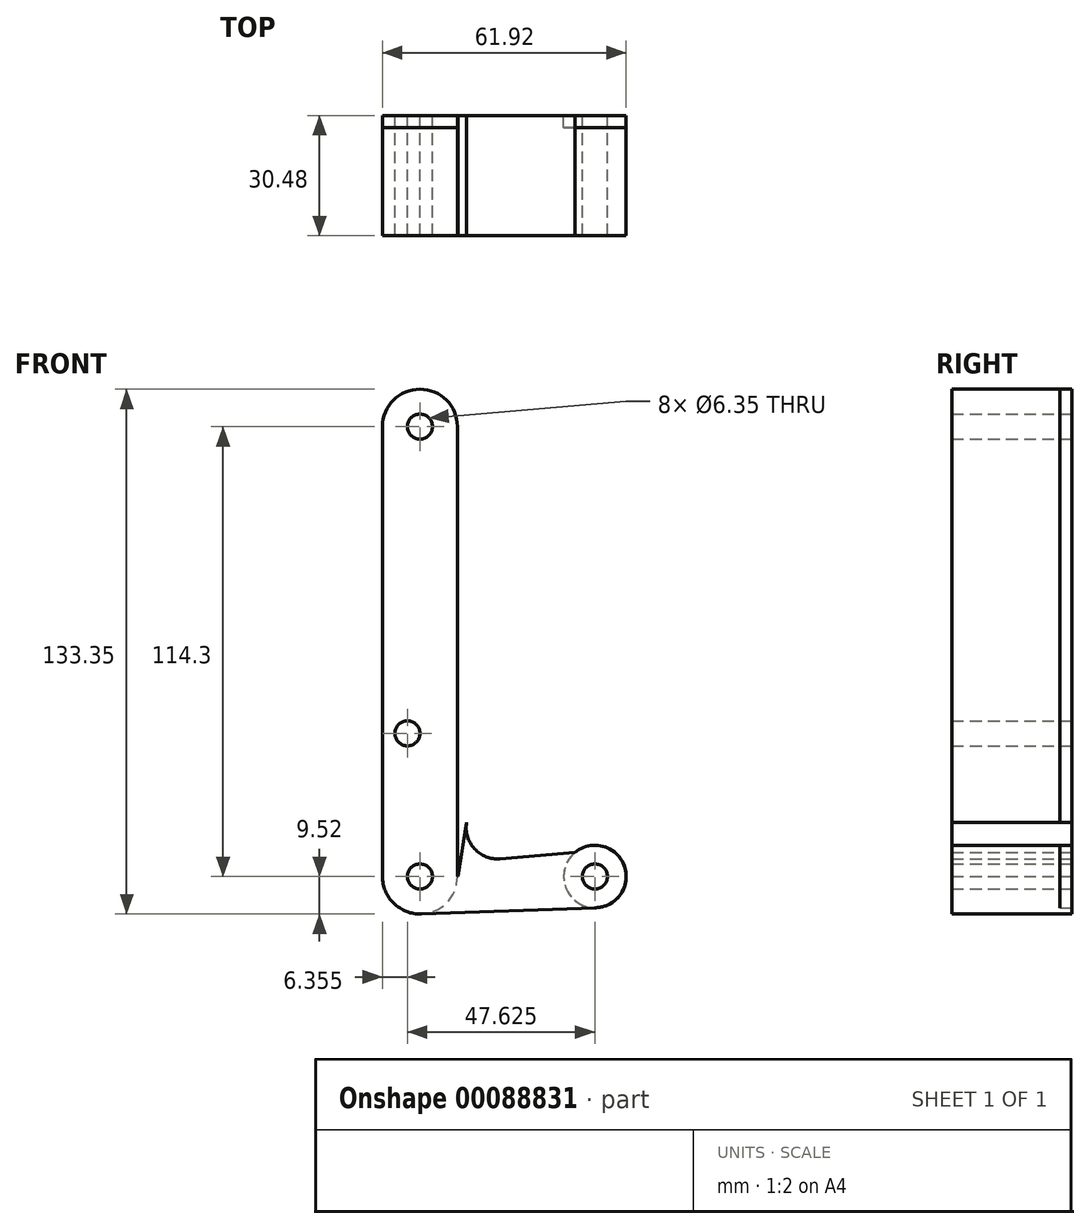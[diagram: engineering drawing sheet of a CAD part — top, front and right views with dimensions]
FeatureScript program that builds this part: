
annotation { "Feature Type Name" : "Feature", "Feature Type Description" : "" }
export const myFeature = defineFeature(function(context is Context, id is Id, definition is map)
    precondition{}
    {
        {
            var Q0;
            Q0=qCreatedBy(makeId("Front.planeOp"),FACE);
            var sketch = newSketch(context, id + "F0", { "sketchPlane" : qUnion([Q0])});
            skCircle(sketch, "E0", {"center": v(0, 114.3) * mm, "radius": 9.53 * mm});
            skCircle(sketch, "E1", {"center": v(0, 0) * mm, "radius": 9.53 * mm});
            skLineSegment(sketch, "E2", {"start": v(0, 114.3) * mm, "end": v(0, 0) * mm, "construction": true});
            skLineSegment(sketch, "E3", {"start": v(0, 0) * mm, "end": v(0, 0) * mm});
            skCircle(sketch, "E4", {"center": v(44.45, 0) * mm, "radius": 7.94 * mm});
            skLineSegment(sketch, "E5", {"start": v(0, 0) * mm, "end": v(44.45, 0) * mm, "construction": true});
            skLineSegment(sketch, "E6", {"start": v(-9.53, 114.3) * mm, "end": v(9.53, 114.3) * mm, "construction": true});
            skLineSegment(sketch, "E7", {"start": v(36.51, 0) * mm, "end": v(52.39, 0) * mm, "construction": true});
            skCircle(sketch, "E8", {"center": v(-3.17, 36.39) * mm, "radius": 3.18 * mm});
            skCircle(sketch, "E9", {"center": v(0, 114.3) * mm, "radius": 3.18 * mm});
            skCircle(sketch, "E10", {"center": v(0, 0) * mm, "radius": 3.18 * mm});
            skCircle(sketch, "E11", {"center": v(44.45, 0) * mm, "radius": 3.18 * mm});
            skLineSegment(sketch, "E12", {"start": v(0, 0) * mm, "end": v(-9.52, 0) * mm, "construction": true});
            skLineSegment(sketch, "E13", {"start": v(44.45, 0) * mm, "end": v(44.45, 7.94) * mm, "construction": true});
            skLineSegment(sketch, "E14", {"start": v(44.45, 0) * mm, "end": v(44.45, -7.94) * mm, "construction": true});
            skLineSegment(sketch, "E15", {"start": v(0, 0) * mm, "end": v(0, -9.52) * mm, "construction": true});
            skLineSegment(sketch, "E16", {"start": v(-9.48, -0.95) * mm, "end": v(-9.48, -0.95) * mm});
            skLineSegment(sketch, "E17", {"start": v(-9.53, 0) * mm, "end": v(-9.53, 114.3) * mm});
            skLineSegment(sketch, "E18", {"start": v(9.52, 114.3) * mm, "end": v(9.53, 0) * mm});
            skLineSegment(sketch, "E19", {"start": v(0.34, -9.52) * mm, "end": v(44.73, -7.93) * mm});
            skLineSegment(sketch, "E20", {"start": v(-29.5, 0) * mm, "end": v(-9.52, 0) * mm, "construction": true});
            skLineSegment(sketch, "E21", {"start": v(-9.53, 0) * mm, "end": v(15.62, 0) * mm});
            skLineSegment(sketch, "E22", {"start": v(11.85, 13.7) * mm, "end": v(9.4, -1.51) * mm});
            skLineSegment(sketch, "E23", {"start": v(20.37, 4.51) * mm, "end": v(39.39, 6.11) * mm});
            skArc(sketch, "E24.filletArc", {"start": v(11.85, 13.7) * mm, "mid": v(13.87, 7.03) * mm, "end": v(20.37, 4.51) * mm});
            skSolve(sketch);
        }
        {
            var Q0;
            {var subQ0=sQuery(id+"F0.wireOp",EDGE,"WO3eCZr5-fNXB-MPyK-c7Pb-Blm2dAQ9tnTr");var subQ1=sQuery(id+"F0.wireOp",EDGE,"E1");var subQ3=makeQuery(id+"F0.imprint","INTERSECT",VERTEX,{"derivedFrom":[subQ1,subQ0]});Q0=makeQuery(id+"F0.imprint","IMPRINT",FACE,{"disambiguationData":[TD([[makeQuery(id+"F0.imprint","IMPRINT",EDGE,{"disambiguationData":[TD([[subQ3,-1.0]])],"derivedFrom":subQ1}),1.0]])]});}
            var Q1;
            {var subQ0=sQuery(id+"F0.wireOp",EDGE,"HDLuu1hv-UhLx-1RbK-1B1E-SFA8OtgyVLiV");var subQ1=sQuery(id+"F0.wireOp",EDGE,"E1");var subQ3=makeQuery(id+"F0.imprint","INTERSECT",VERTEX,{"derivedFrom":[subQ1,subQ0]});Q1=makeQuery(id+"F0.imprint","IMPRINT",FACE,{"disambiguationData":[TD([[makeQuery(id+"F0.imprint","IMPRINT",EDGE,{"disambiguationData":[TD([[subQ3,1.0]])],"derivedFrom":subQ1}),1.0]])]});}
            var Q2;
            Q2=makeQuery(id+"F0.imprint","IMPRINT",FACE,{"disambiguationData":[TD([[makeQuery(id+"F0.imprint","IMPRINT",EDGE,{"derivedFrom":sQuery(id+"F0.wireOp",EDGE,"E9")}),-1.0]])]});
            var Q3;
            Q3=makeQuery(id+"F0.imprint","IMPRINT",FACE,{"disambiguationData":[TD([[makeQuery(id+"F0.imprint","IMPRINT",EDGE,{"derivedFrom":sQuery(id+"F0.wireOp",EDGE,"E10")}),-1.0]])]});
            var Q4;
            Q4=makeQuery(id+"F0.imprint","IMPRINT",FACE,{"disambiguationData":[TD([[makeQuery(id+"F0.imprint","IMPRINT",EDGE,{"derivedFrom":sQuery(id+"F0.wireOp",EDGE,"E11")}),-1.0]])]});
            var Q5;
            {var subQ0=sQuery(id+"F0.wireOp",EDGE,"WrntBw47-ybk8-7ETv-zcuC-ZTsZzzl9P6jG");Q5=makeQuery(id+"F0.imprint","IMPRINT",FACE,{"disambiguationData":[TD([[makeQuery(id+"F0.imprint","IMPRINT",EDGE,{"derivedFrom":subQ0}),-1.0]])]});}
            var Q6;
            Q6=makeQuery(id+"F0.imprint","IMPRINT",FACE,{"disambiguationData":[TD([[makeQuery(id+"F0.imprint","IMPRINT",EDGE,{"derivedFrom":sQuery(id+"F0.wireOp",EDGE,"E8")}),-1.0]])]});
            var Q7;
            Q7=makeQuery(id+"F0.imprint","IMPRINT",FACE,{"disambiguationData":[TD([[makeQuery(id+"F0.imprint","IMPRINT",EDGE,{"derivedFrom":sQuery(id+"F0.wireOp",EDGE,"E10")}),-1.0]])]});
            extrude(context, id + "F1", {"entities" : qUnion([Q0, Q1, Q2, Q3, Q4, Q5, Q6, Q7]), "depth" : 3.05 * mm});
        }
        {
            var Q0;
            Q0 = qSketchRegion(id + "F0", true);
            extrude(context, id + "F2", {"entities" : qUnion([Q0]), "depth" : 30.48 * mm});
        }
    });
